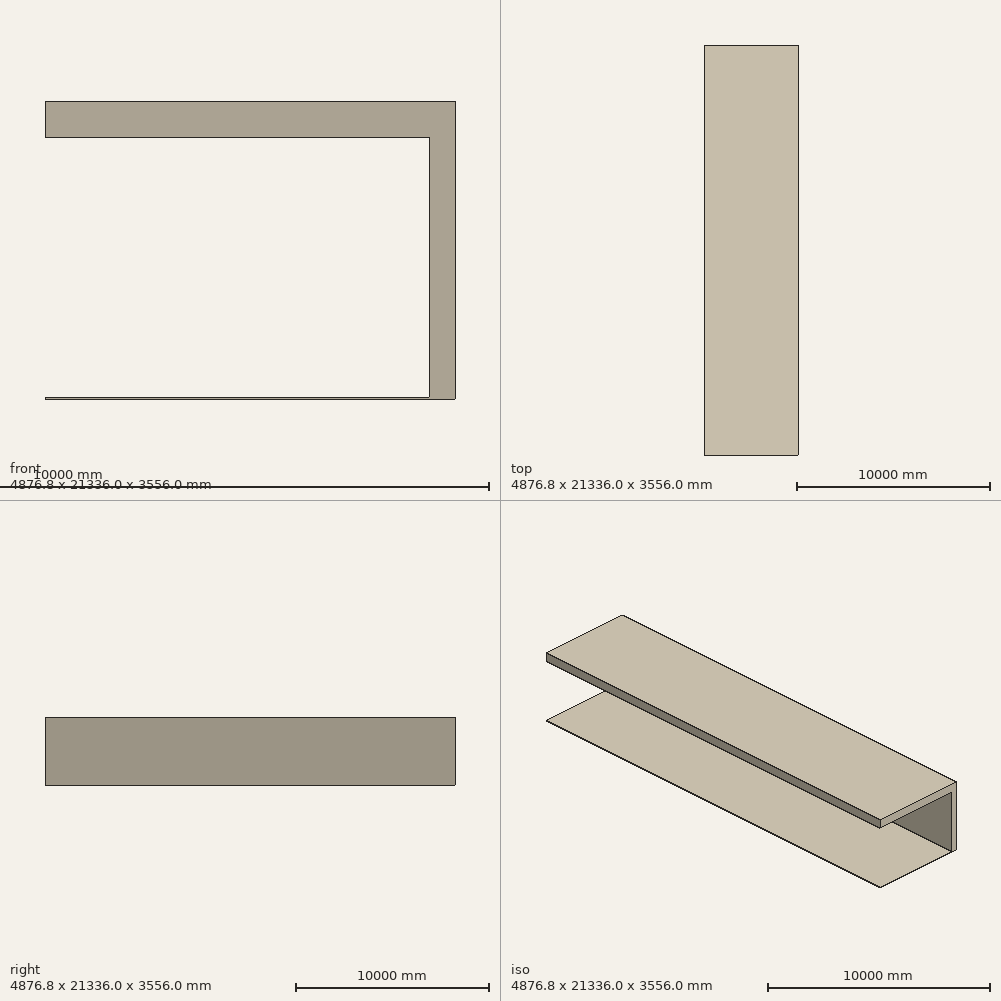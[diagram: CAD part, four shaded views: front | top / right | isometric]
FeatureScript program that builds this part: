
annotation { "Feature Type Name" : "Feature", "Feature Type Description" : "" }
export const myFeature = defineFeature(function(context is Context, id is Id, definition is map)
    precondition{}
    {
        {
            var Q0;
            Q0=qCreatedBy(makeId("Front.planeOp"),FACE);
            var sketch = newSketch(context, id + "F0", { "sketchPlane" : qUnion([Q0])});
            skLineSegment(sketch, "E0.bottom", {"start": v(-2285.12, 1782.4) * mm, "end": v(2591.68, 1782.4) * mm});
            skLineSegment(sketch, "E0.top", {"start": v(-2285.12, -1773.6) * mm, "end": v(2591.68, -1773.6) * mm});
            skLineSegment(sketch, "E0.left", {"start": v(-2285.12, 1782.4) * mm, "end": v(-2285.12, -1773.6) * mm});
            skLineSegment(sketch, "E0.right", {"start": v(2591.68, 1782.4) * mm, "end": v(2591.68, -1773.6) * mm});
            skSolve(sketch);
        }
        {
            var Q0;
            Q0 = qSketchRegion(id + "F0", true);
            extrude(context, id + "F1", {"entities" : qUnion([Q0]), "depth" : 15240 * mm, "offsetDistance" : 25.4 * mm});
        }
        {
            var Q0;
            Q0=makeQuery(id+"F1.opExtrude","CAP_FACE",FACE,{"disambiguationData":[OSD([sQuery(id+"F0.wireOp",EDGE,"E0.bottom"),sQuery(id+"F0.wireOp",EDGE,"E0.top"),sQuery(id+"F0.wireOp",EDGE,"E0.left"),sQuery(id+"F0.wireOp",EDGE,"E0.right")])],"isStart":false});
            var sketch = newSketch(context, id + "F2", { "sketchPlane" : qUnion([Q0])});
            skLineSegment(sketch, "E1.bottom", {"start": v(-2285.12, -1748.2) * mm, "end": v(2286.88, -1748.2) * mm});
            skLineSegment(sketch, "E1.top", {"start": v(-2285.12, 1350.6) * mm, "end": v(2286.88, 1350.6) * mm});
            skLineSegment(sketch, "E1.left", {"start": v(-2285.12, -1748.2) * mm, "end": v(-2285.12, 1350.6) * mm});
            skLineSegment(sketch, "E1.right", {"start": v(2286.88, -1748.2) * mm, "end": v(2286.88, 1350.6) * mm});
            skSolve(sketch);
        }
        {
            var Q0;
            Q0 = qSketchRegion(id + "F2", true);
            extrude(context, id + "F3", {"entities" : qUnion([Q0]), "operationType" : NewBodyOperationType.REMOVE, "oppositeDirection" : true, "depth" : 21285.2 * mm, "offsetDistance" : 25.4 * mm});
        }
        {
            var Q0;
            Q0=makeQuery(id+"F1.opExtrude","CAP_FACE",FACE,{"disambiguationData":[OSD([sQuery(id+"F0.wireOp",EDGE,"E0.bottom"),sQuery(id+"F0.wireOp",EDGE,"E0.top"),sQuery(id+"F0.wireOp",EDGE,"E0.left"),sQuery(id+"F0.wireOp",EDGE,"E0.right")])],"isStart":true});
            extrude(context, id + "F4", {"entities" : qUnion([Q0]), "operationType" : NewBodyOperationType.ADD, "depth" : 6096 * mm, "offsetDistance" : 25.4 * mm});
        }
    });
